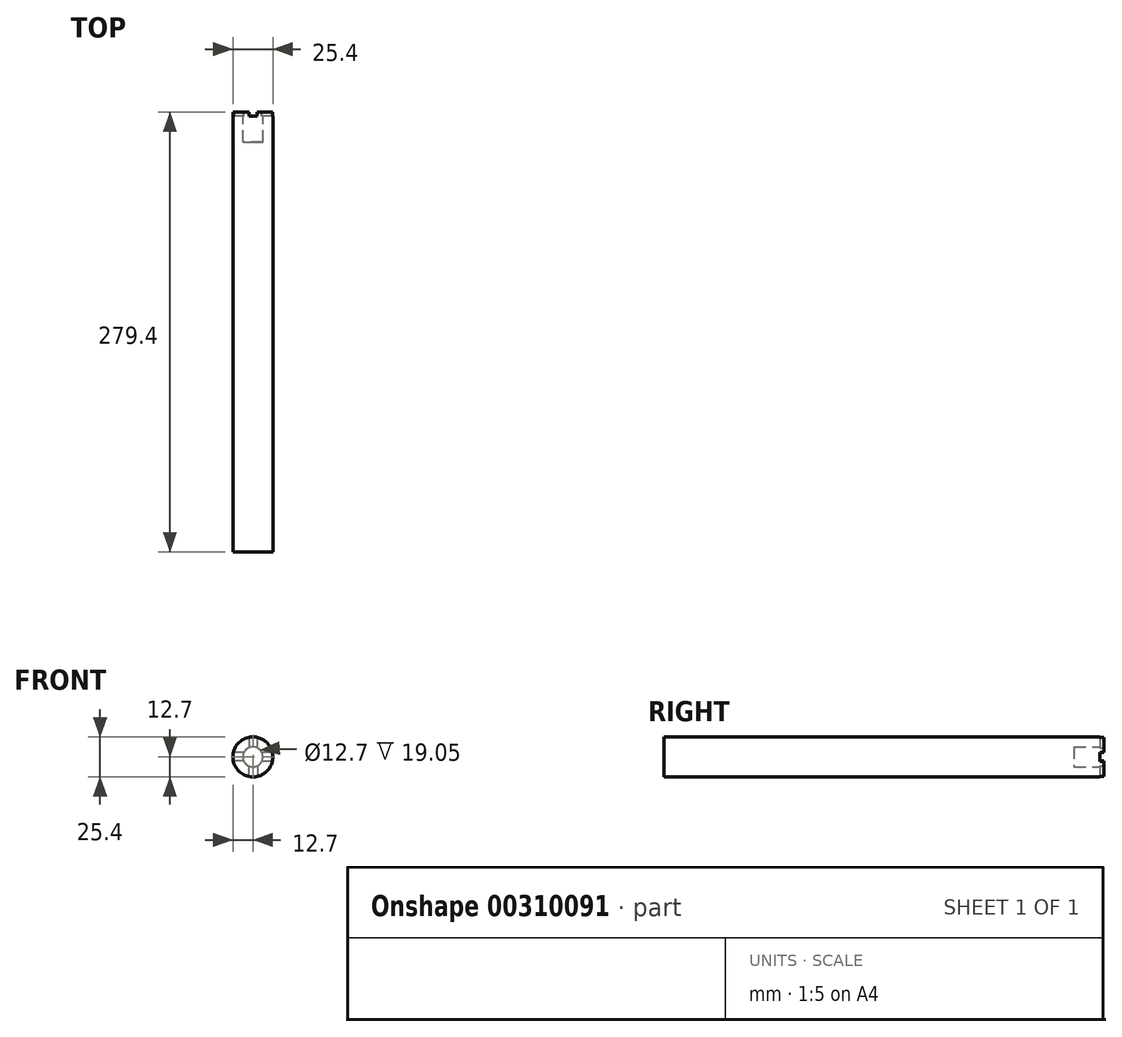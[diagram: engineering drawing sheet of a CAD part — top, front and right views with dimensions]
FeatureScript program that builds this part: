
annotation { "Feature Type Name" : "Feature", "Feature Type Description" : "" }
export const myFeature = defineFeature(function(context is Context, id is Id, definition is map)
    precondition{}
    {
        {
            var Q0;
            Q0=qCreatedBy(makeId("Front.planeOp"),FACE);
            var sketch = newSketch(context, id + "F0", { "sketchPlane" : qUnion([Q0])});
            skCircle(sketch, "E0", {"center": v(0, 0) * mm, "radius": 12.7 * mm});
            skSolve(sketch);
        }
        {
            var Q0;
            Q0 = qSketchRegion(id + "F0", true);
            extrude(context, id + "F1", {"entities" : qUnion([Q0]), "depth" : 279.4 * mm});
        }
        {
            var Q0;
            Q0=makeQuery(id+"F1.opExtrude","CAP_FACE",FACE,{"disambiguationData":[OSD([sQuery(id+"F0.wireOp",EDGE,"E0")])],"isStart":true});
            var sketch = newSketch(context, id + "F2", { "sketchPlane" : qUnion([Q0])});
            skCircle(sketch, "E1", {"center": v(0, 0) * mm, "radius": 6.35 * mm});
            skSolve(sketch);
        }
        {
            var Q0;
            Q0 = qSketchRegion(id + "F2", true);
            extrude(context, id + "F3", {"entities" : qUnion([Q0]), "operationType" : NewBodyOperationType.REMOVE, "oppositeDirection" : true, "depth" : 19.05 * mm});
        }
        {
            var Q0;
            Q0=qCreatedBy(makeId("Front.planeOp"),FACE);
            var sketch = newSketch(context, id + "F4", { "sketchPlane" : qUnion([Q0])});
            skLineSegment(sketch, "E2.bottom", {"start": v(2.56, 16) * mm, "end": v(-2.52, 16) * mm});
            skLineSegment(sketch, "E2.top", {"start": v(2.56, 5.62) * mm, "end": v(-2.52, 5.62) * mm});
            skLineSegment(sketch, "E2.left", {"start": v(2.56, 16) * mm, "end": v(2.56, 5.62) * mm});
            skLineSegment(sketch, "E2.right", {"start": v(-2.52, 16) * mm, "end": v(-2.52, 5.62) * mm});
            skLineSegment(sketch, "E3.bottom", {"start": v(-5, -2.53) * mm, "end": v(-16.26, -2.53) * mm});
            skLineSegment(sketch, "E3.top", {"start": v(-5, 2.85) * mm, "end": v(-16.26, 2.85) * mm});
            skLineSegment(sketch, "E3.left", {"start": v(-5, -2.53) * mm, "end": v(-5, 2.85) * mm});
            skLineSegment(sketch, "E3.right", {"start": v(-16.26, -2.53) * mm, "end": v(-16.26, 2.85) * mm});
            skLineSegment(sketch, "E4.bottom", {"start": v(2.86, -4.95) * mm, "end": v(-2.82, -4.95) * mm});
            skLineSegment(sketch, "E4.top", {"start": v(2.86, -14.48) * mm, "end": v(-2.82, -14.48) * mm});
            skLineSegment(sketch, "E4.left", {"start": v(2.86, -4.95) * mm, "end": v(2.86, -14.48) * mm});
            skLineSegment(sketch, "E4.right", {"start": v(-2.82, -4.95) * mm, "end": v(-2.82, -14.48) * mm});
            skLineSegment(sketch, "E5.bottom", {"start": v(16.01, 2.85) * mm, "end": v(5.18, 2.85) * mm});
            skLineSegment(sketch, "E5.top", {"start": v(16.01, -2.83) * mm, "end": v(5.18, -2.83) * mm});
            skLineSegment(sketch, "E5.left", {"start": v(16.01, 2.85) * mm, "end": v(16.01, -2.83) * mm});
            skLineSegment(sketch, "E5.right", {"start": v(5.18, 2.85) * mm, "end": v(5.18, -2.83) * mm});
            skSolve(sketch);
        }
        {
            var Q0;
            Q0 = qSketchRegion(id + "F4", true);
            extrude(context, id + "F5", {"entities" : qUnion([Q0]), "operationType" : NewBodyOperationType.REMOVE, "depth" : 2.54 * mm});
        }
    });
